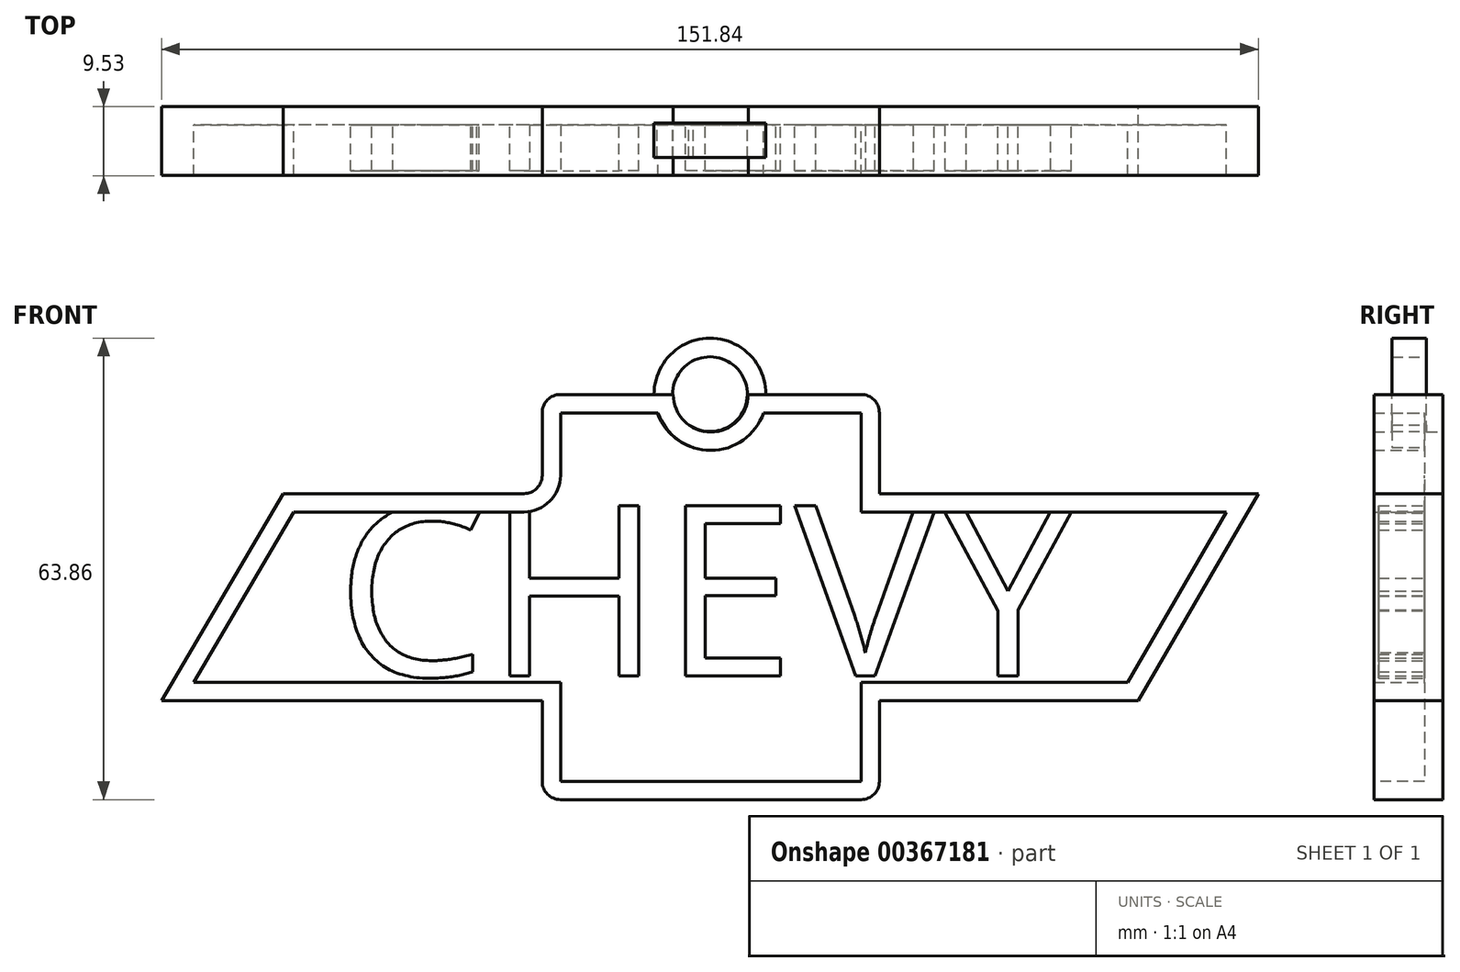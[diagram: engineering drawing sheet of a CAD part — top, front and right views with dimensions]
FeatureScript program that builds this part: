
annotation { "Feature Type Name" : "Feature", "Feature Type Description" : "" }
export const myFeature = defineFeature(function(context is Context, id is Id, definition is map)
    precondition{}
    {
        {
            var Q0;
            Q0=qCreatedBy(makeId("Front.planeOp"),FACE);
            var sketch = newSketch(context, id + "F0", { "sketchPlane" : qUnion([Q0])});
            skLineSegment(sketch, "E0.bottom", {"start": v(59.2, 14.32) * mm, "end": v(23.34, 14.32) * mm});
            skLineSegment(sketch, "E0.top", {"start": v(59.2, -14.32) * mm, "end": v(23.34, -14.32) * mm});
            skPoint(sketch, "E0.middle", {"position": v(0, 0) * mm});
            skLineSegment(sketch, "E1.bottom", {"start": v(23.34, 28.03) * mm, "end": v(5.42, 28.03) * mm});
            skLineSegment(sketch, "E1.top", {"start": v(23.34, -28.03) * mm, "end": v(-23.34, -28.03) * mm});
            skLineSegment(sketch, "E1.left", {"start": v(23.34, 28.03) * mm, "end": v(23.34, 14.32) * mm});
            skLineSegment(sketch, "E1.right", {"start": v(-23.34, 28.03) * mm, "end": v(-23.34, 14.32) * mm});
            skLineSegment(sketch, "E2", {"start": v(59.2, 14.32) * mm, "end": v(75.8, 14.32) * mm});
            skLineSegment(sketch, "E3", {"start": v(75.8, 14.32) * mm, "end": v(59.2, -14.32) * mm});
            skLineSegment(sketch, "E4", {"start": v(-59.2, -14.32) * mm, "end": v(-76.04, -14.32) * mm});
            skLineSegment(sketch, "E5", {"start": v(-76.04, -14.32) * mm, "end": v(-59.2, 14.32) * mm});
            skLineSegment(sketch, "E6.trimOffspring", {"start": v(23.34, -14.32) * mm, "end": v(23.34, -28.03) * mm});
            skLineSegment(sketch, "E7.trimOffspring", {"start": v(-23.34, 14.32) * mm, "end": v(-59.2, 14.32) * mm});
            skLineSegment(sketch, "E8.trimOffspring", {"start": v(-23.34, -14.32) * mm, "end": v(-23.34, -28.03) * mm});
            skLineSegment(sketch, "E9.trimOffspring", {"start": v(-23.34, -14.32) * mm, "end": v(-59.2, -14.32) * mm});
            skLineSegment(sketch, "E10.trimOffspring", {"start": v(-6.5, 28.03) * mm, "end": v(-23.34, 28.03) * mm});
            skLineSegment(sketch, "E11.trimOffspring", {"start": v(5.42, 28.03) * mm, "end": v(6.26, 28.03) * mm});
            skLineSegment(sketch, "E12", {"start": v(-6.5, 28.03) * mm, "end": v(-5.2, 28.03) * mm});
            skCircle(sketch, "E13", {"center": v(0, 28.03) * mm, "radius": 3.13 * mm});
            skCircle(sketch, "E14", {"center": v(0, 28.03) * mm, "radius": 5.2 * mm});
            skLineSegment(sketch, "E15.trimOffspring", {"start": v(5.2, 28.03) * mm, "end": v(6.26, 28.03) * mm});
            skSolve(sketch);
        }
        {
            var Q0;
            Q0=makeQuery(id+"F0.imprint","IMPRINT",FACE,{"disambiguationData":[TD([[makeQuery(id+"F0.imprint","IMPRINT",EDGE,{"derivedFrom":sQuery(id+"F0.wireOp",EDGE,"E0.bottom")}),1.0]])]});
            extrude(context, id + "F1", {"entities" : qUnion([Q0]), "depth" : 9.52 * mm});
        }
        {
            var Q0;
            Q0=makeQuery(id+"F1.opExtrude","SWEPT_EDGE",EDGE,{"disambiguationData":[OSD([sQuery(id+"F0.wireOp",EDGE,"E1.bottom"),sQuery(id+"F0.wireOp",EDGE,"E1.left")])]});
            var Q1;
            Q1=makeQuery(id+"F1.opExtrude","SWEPT_EDGE",EDGE,{"disambiguationData":[OSD([sQuery(id+"F0.wireOp",EDGE,"E1.bottom"),sQuery(id+"F0.wireOp",EDGE,"E1.right")])]});
            var Q2;
            Q2=makeQuery(id+"F1.opExtrude","SWEPT_EDGE",EDGE,{"disambiguationData":[OSD([sQuery(id+"F0.wireOp",EDGE,"E1.top"),sQuery(id+"F0.wireOp",EDGE,"E6.trimOffspring")])]});
            var Q3;
            Q3=makeQuery(id+"F1.opExtrude","SWEPT_EDGE",EDGE,{"disambiguationData":[OSD([sQuery(id+"F0.wireOp",EDGE,"E1.top"),sQuery(id+"F0.wireOp",EDGE,"E8.trimOffspring")])]});
            fillet(context, id + "F2", {"entities" : qUnion([Q0, Q1, Q2, Q3]), "radius" : 2.54 * mm, "tangentPropagation" : true, "allowEdgeOverflow" : false});
        }
        {
            var Q0;
            Q0=makeQuery(id+"F1.opExtrude","CAP_FACE",FACE,{"disambiguationData":[OSD([sQuery(id+"F0.wireOp",EDGE,"E0.bottom"),sQuery(id+"F0.wireOp",EDGE,"E0.top"),sQuery(id+"F0.wireOp",EDGE,"E1.bottom"),sQuery(id+"F0.wireOp",EDGE,"E1.top"),sQuery(id+"F0.wireOp",EDGE,"E1.left"),sQuery(id+"F0.wireOp",EDGE,"E1.right"),sQuery(id+"F0.wireOp",EDGE,"E2"),sQuery(id+"F0.wireOp",EDGE,"E3"),sQuery(id+"F0.wireOp",EDGE,"E4"),sQuery(id+"F0.wireOp",EDGE,"E5"),sQuery(id+"F0.wireOp",EDGE,"E6.trimOffspring"),sQuery(id+"F0.wireOp",EDGE,"E7.trimOffspring"),sQuery(id+"F0.wireOp",EDGE,"E8.trimOffspring"),sQuery(id+"F0.wireOp",EDGE,"E9.trimOffspring")])],"isStart":false});
            shell(context, id + "F3", {"entities" : qUnion([Q0]), "thickness" : 2.54 * mm});
        }
        {
            var Q0;
            Q0=makeQuery(id+"F3.opShell","OFFSET_FACE",FACE,{"disambiguationData":[OSD([sQuery(id+"F0.wireOp",EDGE,"E0.bottom"),sQuery(id+"F0.wireOp",EDGE,"E0.top"),sQuery(id+"F0.wireOp",EDGE,"E1.bottom"),sQuery(id+"F0.wireOp",EDGE,"E1.top"),sQuery(id+"F0.wireOp",EDGE,"E1.left"),sQuery(id+"F0.wireOp",EDGE,"E1.right"),sQuery(id+"F0.wireOp",EDGE,"E2"),sQuery(id+"F0.wireOp",EDGE,"E3"),sQuery(id+"F0.wireOp",EDGE,"E4"),sQuery(id+"F0.wireOp",EDGE,"E5"),sQuery(id+"F0.wireOp",EDGE,"E6.trimOffspring"),sQuery(id+"F0.wireOp",EDGE,"E7.trimOffspring"),sQuery(id+"F0.wireOp",EDGE,"E8.trimOffspring"),sQuery(id+"F0.wireOp",EDGE,"E9.trimOffspring")])]});
            var sketch = newSketch(context, id + "F4", { "sketchPlane" : qUnion([Q0])});
            skSolve(sketch);
        }
        {
            var Q0;
            Q0=qCreatedBy(makeId("Front.planeOp"),FACE);
            cPlane(context, id + "F5", {"entities" : qUnion([Q0]), "cplaneType" : CPlaneType.OFFSET, "offset" : 4.64 * mm, "width" : 152.4 * mm, "height" : 152.4 * mm});
        }
        {
            var Q0;
            Q0=qCreatedBy(id+"F5.planeOp",FACE);
            var sketch = newSketch(context, id + "F6", { "sketchPlane" : qUnion([Q0])});
            skLineSegment(sketch, "E16", {"start": v(-5.3, 28.08) * mm, "end": v(-5.28, 28.08) * mm});
            skCircle(sketch, "E17", {"center": v(-0.1, 28.08) * mm, "radius": 5.17 * mm});
            skCircle(sketch, "E18", {"center": v(-0.1, 28.08) * mm, "radius": 7.75 * mm});
            skLineSegment(sketch, "E19.trimOffspring", {"start": v(-0.1, 28.08) * mm, "end": v(0, 28.08) * mm});
            skLineSegment(sketch, "E20.trimOffspring", {"start": v(5.06, 28.08) * mm, "end": v(5.09, 28.08) * mm});
            skSolve(sketch);
        }
        {
            var Q0;
            Q0=makeQuery(id+"F6.imprint","IMPRINT",FACE,{"disambiguationData":[TD([[makeQuery(id+"F6.imprint","IMPRINT",EDGE,{"derivedFrom":sQuery(id+"F6.wireOp",EDGE,"E18")}),1.0]])]});
            extrude(context, id + "F7", {"entities" : qUnion([Q0]), "operationType" : NewBodyOperationType.ADD, "endBound" : BoundingType.SYMMETRIC, "depth" : 4.76 * mm});
        }
        {
            var Q0;
            {var subQ16=sQuery(id+"F0.wireOp",EDGE,"E0.top");Q0=makeQuery(id+"F4.imprint","IMPRINT",FACE,{"disambiguationData":[TD([[makeQuery(id+"F4.imprint","IMPRINT",EDGE,{"derivedFrom":makeQuery(id+"F3.opShell","OFFSET_EDGE",EDGE,{"disambiguationData":[OSD([subQ16]),TDD([makeQuery(id+"F1.opExtrude","CAP_EDGE",EDGE,{"disambiguationData":[OSD([subQ16])],"isStart":true})])]})}),-1.0]])]});}
            var sketch = newSketch(context, id + "F8", { "sketchPlane" : qUnion([Q0])});
            skText(sketch, "E21", { "text": "CHEVY\n", "fontName": "OpenSans-Regular.ttf"});
            const initialGuessF8  = {"E21": [-0.05186, -0.01091, 1, 0, 0.02374]};
            skSetInitialGuess(sketch, initialGuessF8);
            skSolve(sketch);
        }
        {
            var Q0;
            Q0 = qSketchRegion(id + "F8", true);
            extrude(context, id + "F9", {"entities" : qUnion([Q0]), "operationType" : NewBodyOperationType.ADD, "depth" : 6.35 * mm});
        }
    });
